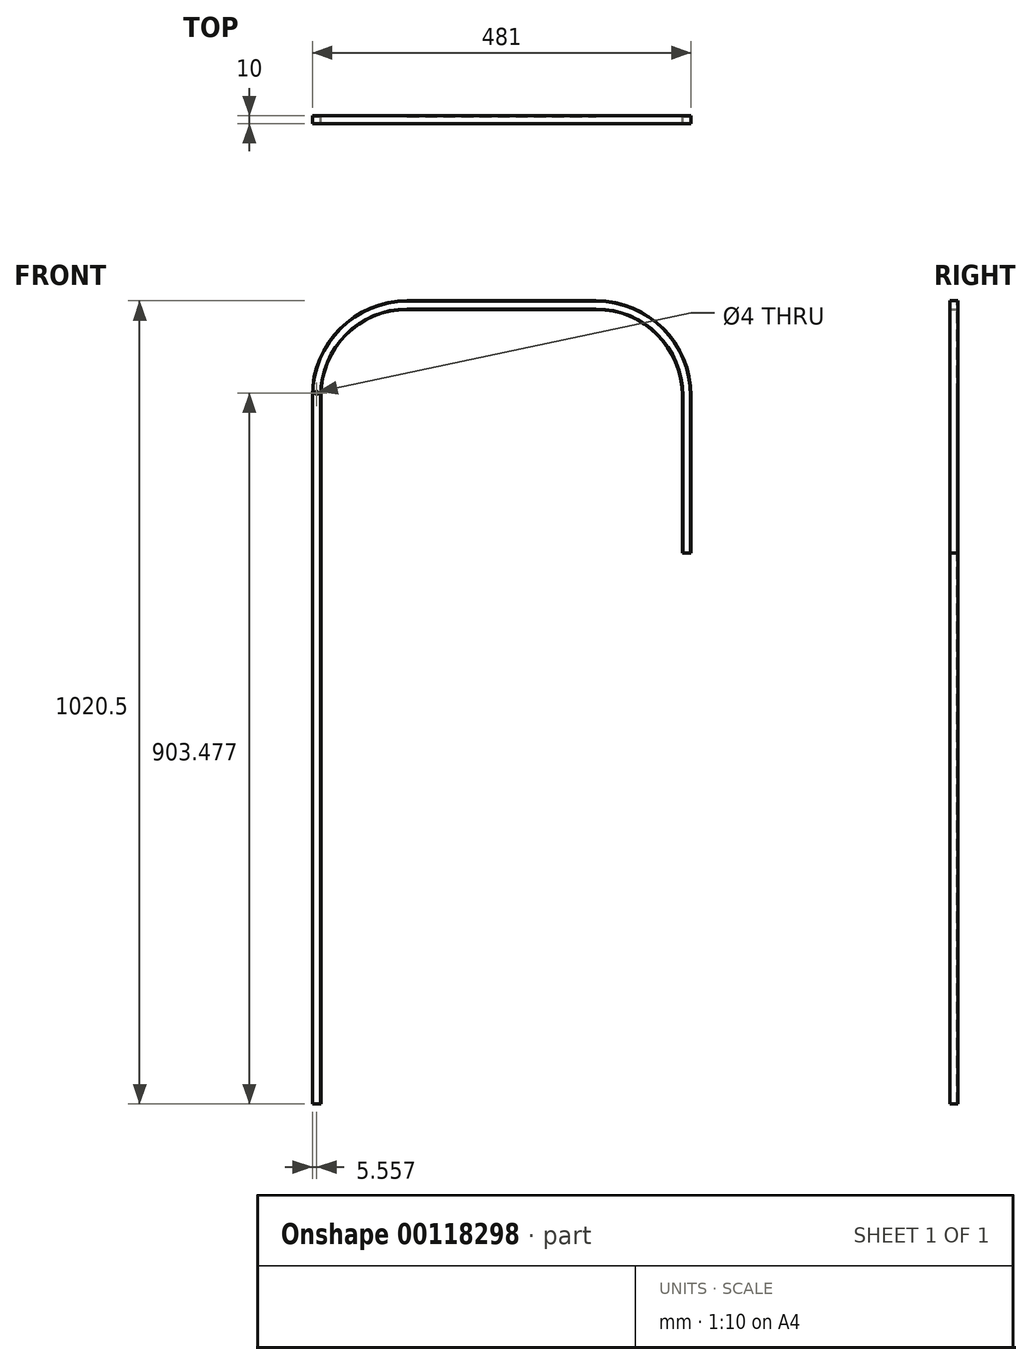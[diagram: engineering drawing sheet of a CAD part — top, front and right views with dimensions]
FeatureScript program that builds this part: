
annotation { "Feature Type Name" : "Feature", "Feature Type Description" : "" }
export const myFeature = defineFeature(function(context is Context, id is Id, definition is map)
    precondition{}
    {
        {
            var Q0;
            Q0=qCreatedBy(makeId("Front.planeOp"),FACE);
            var sketch = newSketch(context, id + "F0", { "sketchPlane" : qUnion([Q0])});
            skLineSegment(sketch, "E0.right", {"start": v(-304.27, 450) * mm, "end": v(-304.27, -450) * mm});
            skPoint(sketch, "E0.middle", {"position": v(15.73, 0) * mm});
            skLineSegment(sketch, "E1", {"start": v(-304.27, 450) * mm, "end": v(-302.77, 450) * mm});
            skLineSegment(sketch, "E2", {"start": v(-302.77, 450) * mm, "end": v(-302.77, 550) * mm});
            skLineSegment(sketch, "E3", {"start": v(-302.77, 550) * mm, "end": v(-272.77, 550) * mm});
            skLineSegment(sketch, "E4", {"start": v(-272.77, 550) * mm, "end": v(-272.77, 580) * mm});
            skLineSegment(sketch, "E5", {"start": v(-272.77, 580) * mm, "end": v(167.23, 580) * mm});
            skLineSegment(sketch, "E6", {"start": v(167.23, 580) * mm, "end": v(167.23, 550) * mm});
            skLineSegment(sketch, "E7", {"start": v(167.23, 550) * mm, "end": v(197.23, 550) * mm});
            skLineSegment(sketch, "E8", {"start": v(197.23, 550) * mm, "end": v(197.23, 450) * mm});
            skLineSegment(sketch, "E9", {"start": v(197.23, 450) * mm, "end": v(198.73, 450) * mm});
            skLineSegment(sketch, "E10", {"start": v(198.73, 450) * mm, "end": v(198.73, -450) * mm});
            skLineSegment(sketch, "E11", {"start": v(-304.27, -450) * mm, "end": v(198.73, -450) * mm});
            skLineSegment(sketch, "E12", {"start": v(-272.77, -450) * mm, "end": v(-304.27, -450) * mm});
            skLineSegment(sketch, "E13", {"start": v(-272.77, 580) * mm, "end": v(-172.77, 580) * mm});
            skLineSegment(sketch, "E14", {"start": v(167.23, 580) * mm, "end": v(67.23, 580) * mm});
            skLineSegment(sketch, "E15", {"start": v(-272.77, -450) * mm, "end": v(-287.77, -450) * mm});
            skLineSegment(sketch, "E16.0.left", {"start": v(-172.77, 570.5) * mm, "end": v(67.23, 570.5) * mm});
            skLineSegment(sketch, "E16.0.right", {"start": v(-172.77, 559.5) * mm, "end": v(67.23, 559.5) * mm});
            skArc(sketch, "E16.1.left", {"start": v(-172.77, 559.5) * mm, "mid": v(-250.2, 527.43) * mm, "end": v(-282.27, 450) * mm});
            skArc(sketch, "E16.1.right", {"start": v(-172.77, 570.5) * mm, "mid": v(-257.97, 535.2) * mm, "end": v(-293.27, 450) * mm});
            skArc(sketch, "E16.2.left", {"start": v(176.73, 450) * mm, "mid": v(144.66, 527.43) * mm, "end": v(67.23, 559.5) * mm});
            skArc(sketch, "E16.2.right", {"start": v(187.73, 450) * mm, "mid": v(152.44, 535.2) * mm, "end": v(67.23, 570.5) * mm});
            skLineSegment(sketch, "E16.3.left", {"start": v(176.73, -450) * mm, "end": v(176.73, 450) * mm});
            skLineSegment(sketch, "E16.3.right", {"start": v(187.73, -450) * mm, "end": v(187.73, 450) * mm});
            skLineSegment(sketch, "E16.4.left", {"start": v(-293.27, -450) * mm, "end": v(-293.27, 450) * mm});
            skLineSegment(sketch, "E16.4.right", {"start": v(-282.27, -450) * mm, "end": v(-282.27, 450) * mm});
            skLineSegment(sketch, "E17.0.left", {"start": v(-292.77, -450) * mm, "end": v(-292.77, 450) * mm});
            skLineSegment(sketch, "E17.0.right", {"start": v(-282.77, -450) * mm, "end": v(-282.77, 450) * mm});
            skArc(sketch, "E17.1.left", {"start": v(-172.77, 560) * mm, "mid": v(-250.55, 527.78) * mm, "end": v(-282.77, 450) * mm});
            skArc(sketch, "E17.1.right", {"start": v(-172.77, 570) * mm, "mid": v(-257.62, 534.85) * mm, "end": v(-292.77, 450) * mm});
            skLineSegment(sketch, "E17.2.left", {"start": v(-172.77, 570) * mm, "end": v(67.23, 570) * mm});
            skLineSegment(sketch, "E17.2.right", {"start": v(-172.77, 560) * mm, "end": v(67.23, 560) * mm});
            skArc(sketch, "E17.3.left", {"start": v(177.23, 450) * mm, "mid": v(145.02, 527.78) * mm, "end": v(67.23, 560) * mm});
            skArc(sketch, "E17.3.right", {"start": v(187.23, 450) * mm, "mid": v(152.09, 534.85) * mm, "end": v(67.23, 570) * mm});
            skLineSegment(sketch, "E17.4.left", {"start": v(177.23, -450) * mm, "end": v(177.23, 450) * mm});
            skLineSegment(sketch, "E17.4.right", {"start": v(187.23, -450) * mm, "end": v(187.23, 450) * mm});
            skSolve(sketch);
        }
        {
            var Q0;
            {var subQ7=sQuery(id+"F0.wireOp",EDGE,"E17.0.left");Q0=makeQuery(id+"F0.imprint","IMPRINT",FACE,{"disambiguationData":[TD([[makeQuery(id+"F0.imprint","IMPRINT",EDGE,{"derivedFrom":subQ7}),-1.0]])]});}
            extrude(context, id + "F1", {"entities" : qUnion([Q0]), "depth" : 1 * mm});
        }
        {
            var Q0;
            Q0=makeQuery(id+"F0.imprint","IMPRINT",FACE,{"disambiguationData":[TD([[makeQuery(id+"F0.imprint","IMPRINT",EDGE,{"derivedFrom":sQuery(id+"F0.wireOp",EDGE,"E16.0.left")}),-1.0]])]});
            var Q1;
            Q1=makeQuery(id+"F0.imprint","IMPRINT",FACE,{"disambiguationData":[TD([[makeQuery(id+"F0.imprint","IMPRINT",EDGE,{"derivedFrom":sQuery(id+"F0.wireOp",EDGE,"E16.0.right")}),1.0]])]});
            extrude(context, id + "F2", {"entities" : qUnion([Q0, Q1]), "operationType" : NewBodyOperationType.ADD, "depth" : 10 * mm});
        }
        {
            var Q0;
            {var subQ0=sQuery(id+"F0.wireOp",EDGE,"E11");Q0=makeQuery(id+"F2.boolean.opBoolean","MERGE",FACE,{"derivedFrom":[makeQuery(id+"F1.opExtrude","SWEPT_FACE",FACE,{"disambiguationData":[OSD([subQ0])]}),makeQuery(id+"F2.opExtrude","SWEPT_FACE",FACE,{"disambiguationData":[OSD([subQ0]),TDD([makeQuery(id+"F0.imprint","IMPRINT",EDGE,{"disambiguationData":[TD([[makeQuery(id+"F0.imprint","INTERSECT",VERTEX,{"derivedFrom":[subQ0,sQuery(id+"F0.wireOp",EDGE,"E16.3.left")]}),-1.0]])],"derivedFrom":subQ0})])]}),makeQuery(id+"F2.opExtrude","SWEPT_FACE",FACE,{"disambiguationData":[OSD([subQ0]),TDD([makeQuery(id+"F0.imprint","IMPRINT",EDGE,{"disambiguationData":[TD([[makeQuery(id+"F0.imprint","INTERSECT",VERTEX,{"derivedFrom":[subQ0,sQuery(id+"F0.wireOp",EDGE,"E16.3.right")]}),1.0]])],"derivedFrom":subQ0})])]})]});}
            extrude(context, id + "F3", {"entities" : qUnion([Q0]), "operationType" : NewBodyOperationType.REMOVE, "oppositeDirection" : true, "depth" : 700 * mm});
        }
        {
            var Q0;
            Q0=makeQuery(id+"F1.opExtrude","CAP_FACE",FACE,{"disambiguationData":[OSD([sQuery(id+"F0.wireOp",EDGE,"E11"),sQuery(id+"F0.wireOp",EDGE,"E12"),sQuery(id+"F0.wireOp",EDGE,"E15"),sQuery(id+"F0.wireOp",EDGE,"E17.0.left"),sQuery(id+"F0.wireOp",EDGE,"E17.0.right"),sQuery(id+"F0.wireOp",EDGE,"E17.1.left"),sQuery(id+"F0.wireOp",EDGE,"E17.1.right"),sQuery(id+"F0.wireOp",EDGE,"E17.2.left"),sQuery(id+"F0.wireOp",EDGE,"E17.2.right"),sQuery(id+"F0.wireOp",EDGE,"E17.3.left"),sQuery(id+"F0.wireOp",EDGE,"E17.3.right"),sQuery(id+"F0.wireOp",EDGE,"E17.4.left"),sQuery(id+"F0.wireOp",EDGE,"E17.4.right")])],"isStart":false});
            var sketch = newSketch(context, id + "F4", { "sketchPlane" : qUnion([Q0])});
            skLineSegment(sketch, "E18", {"start": v(-292.7, 453.9) * mm, "end": v(-282.72, 453.05) * mm});
            skLineSegment(sketch, "E19", {"start": v(-287.71, 453.48) * mm, "end": v(-287.71, 460.6) * mm});
            skSolve(sketch);
        }
        {
            var Q0;
            Q0=sQuery(id+"F4.wireOp",VERTEX,"E19.start");
            var Q1;
            Q1=makeQuery(id+"F1.opExtrude","SWEPT_BODY",BODY,{"disambiguationData":[OSD([sQuery(id+"F0.wireOp",EDGE,"E11"),sQuery(id+"F0.wireOp",EDGE,"E12"),sQuery(id+"F0.wireOp",EDGE,"E15"),sQuery(id+"F0.wireOp",EDGE,"E17.0.left"),sQuery(id+"F0.wireOp",EDGE,"E17.0.right"),sQuery(id+"F0.wireOp",EDGE,"E17.1.left"),sQuery(id+"F0.wireOp",EDGE,"E17.1.right"),sQuery(id+"F0.wireOp",EDGE,"E17.2.left"),sQuery(id+"F0.wireOp",EDGE,"E17.2.right"),sQuery(id+"F0.wireOp",EDGE,"E17.3.left"),sQuery(id+"F0.wireOp",EDGE,"E17.3.right"),sQuery(id+"F0.wireOp",EDGE,"E17.4.left"),sQuery(id+"F0.wireOp",EDGE,"E17.4.right")])]});
            hole(context, id + "F5", {"style" : HoleStyle.SIMPLE, "endStyle" : HoleEndStyle.THROUGH, "holeDiameter" : 4 * mm, "locations" : qUnion([Q0]), "scope" : qUnion([Q1]), "isTappedThrough" : true});
        }
    });
